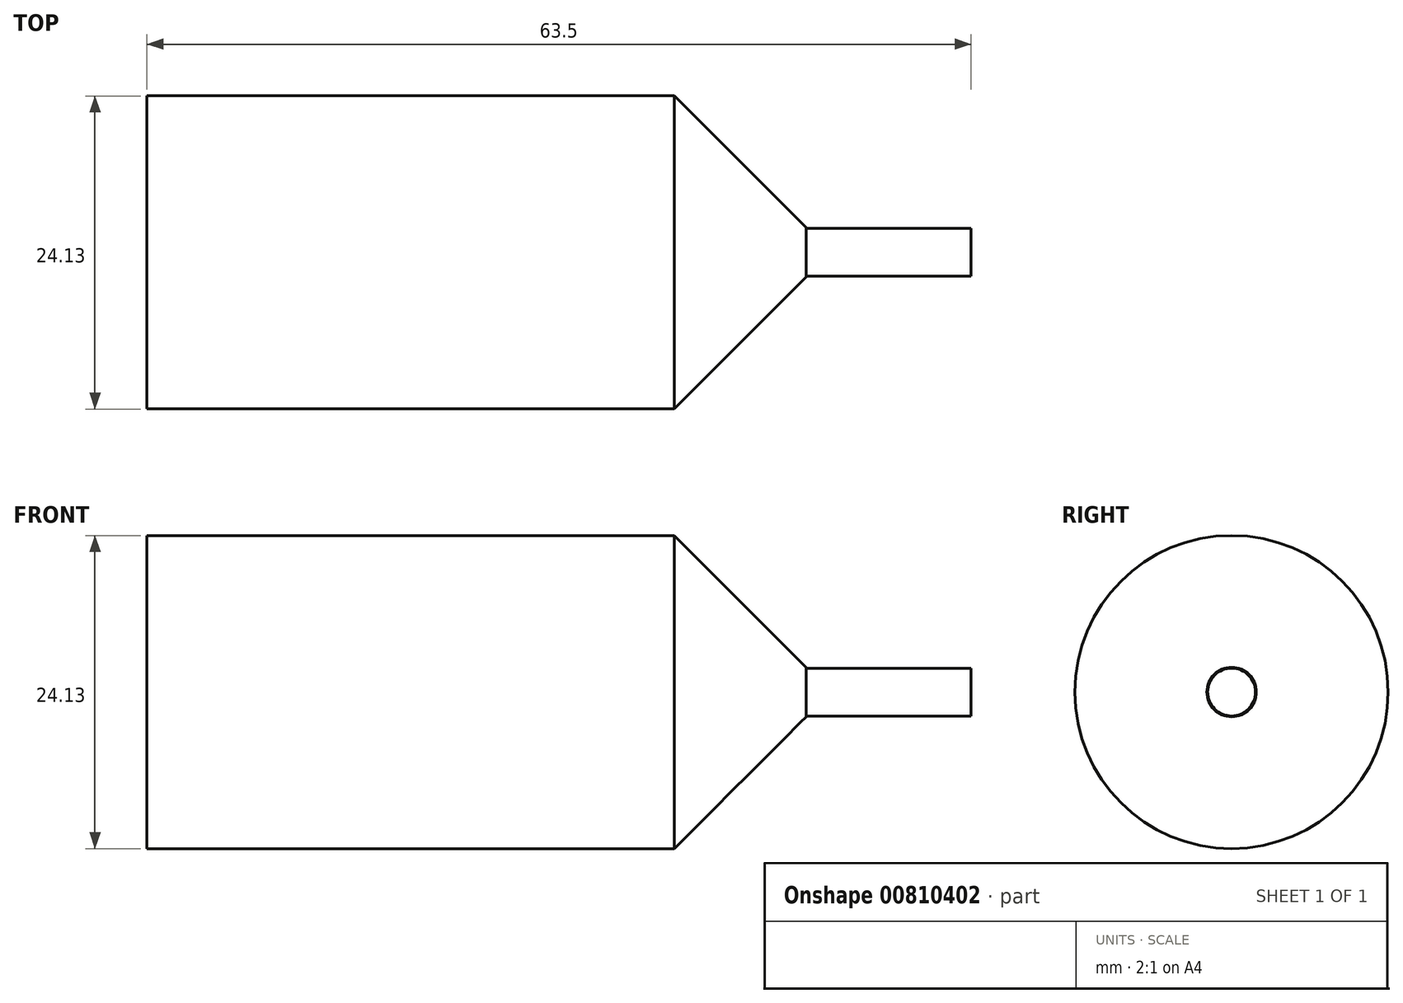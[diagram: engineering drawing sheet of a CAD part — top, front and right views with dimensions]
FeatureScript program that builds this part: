
annotation { "Feature Type Name" : "Feature", "Feature Type Description" : "" }
export const myFeature = defineFeature(function(context is Context, id is Id, definition is map)
    precondition{}
    {
        {
            var Q0;
            Q0=qCreatedBy(makeId("Right.planeOp"),FACE);
            var sketch = newSketch(context, id + "F0", { "sketchPlane" : qUnion([Q0])});
            skCircle(sketch, "E0", {"center": v(-32.94, 30.47) * mm, "radius": 12.06 * mm});
            skSolve(sketch);
        }
        {
            var Q0;
            Q0=makeQuery(id+"F0.imprint","IMPRINT",FACE,{"disambiguationData":[TD([[makeQuery(id+"F0.imprint","IMPRINT",EDGE,{"derivedFrom":sQuery(id+"F0.wireOp",EDGE,"E0")}),1.0]])]});
            extrude(context, id + "F1", {"entities" : qUnion([Q0]), "depth" : 50.8 * mm, "offsetDistance" : 25.4 * mm});
        }
        {
            var Q0;
            Q0=makeQuery(id+"F1.opExtrude","CAP_FACE",FACE,{"disambiguationData":[OSD([sQuery(id+"F0.wireOp",EDGE,"E0")])],"isStart":false});
            var sketch = newSketch(context, id + "F2", { "sketchPlane" : qUnion([Q0])});
            skCircle(sketch, "E1", {"center": v(-32.94, 30.47) * mm, "radius": 1.84 * mm});
            skSolve(sketch);
        }
        {
            var Q0;
            Q0=makeQuery(id+"F2.imprint","IMPRINT",FACE,{"disambiguationData":[TD([[makeQuery(id+"F2.imprint","IMPRINT",EDGE,{"derivedFrom":sQuery(id+"F2.wireOp",EDGE,"E1")}),1.0]])]});
            extrude(context, id + "F3", {"entities" : qUnion([Q0]), "operationType" : NewBodyOperationType.ADD, "depth" : 12.7 * mm, "offsetDistance" : 25.4 * mm});
        }
        {
            var Q0;
            Q0=makeQuery(id+"F1.opExtrude","CAP_EDGE",EDGE,{"disambiguationData":[OSD([sQuery(id+"F0.wireOp",EDGE,"E0")])],"isStart":false});
            chamfer(context, id + "F4", {"entities" : qUnion([Q0]), "width" : 10.16 * mm, "tangentPropagation" : true});
        }
    });
